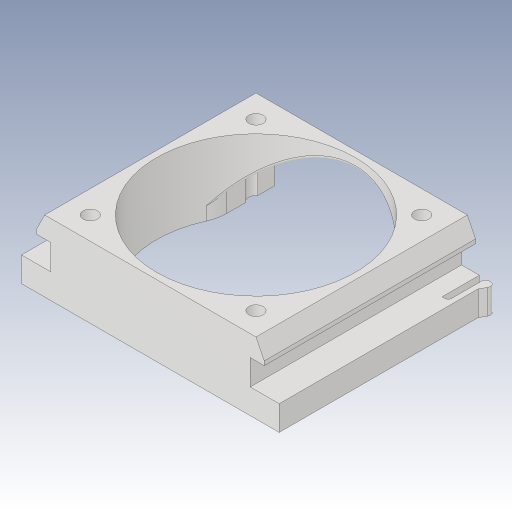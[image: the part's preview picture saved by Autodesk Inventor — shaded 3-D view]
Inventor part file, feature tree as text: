
AUTODESK INVENTOR PART (.ipt)
format: ipt  version: 2023.3 (Build 273359000, 359)  size: 267,264 bytes
history: native  units: in
note: dims shown in document units (in); Inventor stores cm internally (conversion verified against a paired STEP export)
features: extrude x5, sketch x5, fillet x3, plane x2, chamfer x2, hole x1, mirror x1, projected_geometry x1
ambient origin geometry x8: Origin, YZ Plane, XZ Plane, XY Plane, X Axis, Y Axis, Z Axis, Center Point
bodies: Body1 (feature_tree)
feature tree (20):
  extrude  "Extrusion3"  Depth=0.1211in
  plane  "Arbeitsebene1"
  extrude  "Extrusion4"  Depth=0.1378in
  chamfer  "Fase1"  Distance=1.0039in
  extrude  "Extrusion5"  Depth=0.8268in TaperAngle=0.0deg
  fillet  "Rundung1"  Radius=0.962in
  fillet  "Rundung2"  Radius=1.0827in
  hole  "Bohrung1"  [1 undecoded]
  sketch  "Skizze7"  dims[d20=0.9449in d21=0.502in d22=0.7874in d23=0.0in d27=0.1969in d28=0.0157in d29=0.7874in d30=0.0689in d31=0.1969in d32=0.119in d33=0.0787in d34=0.5635in d35=0.248in d36=0.0in d38=0.0531in d39=0.0236in d40=0.0394in d41=0.1772in d42=0.1181in d43=0.0in d44=0.1181in d45=0.0in d46=0.0157in d47=0.0197in d48=0.0787in d49=45.0deg]
  extrude  "Extrusion6"  Depth=0.0197in
  extrude  "Extrusion7"  Depth=0.0197in TaperAngle=0.0deg
  fillet  "Rundung3"  Radius=0.1969in
  plane  "Arbeitsebene2"
  mirror  "Spiegeln1"
  chamfer  "Fase3"  Distance=0.0157in
  sketch  "Skizze3"  dims[d4=0.9488in d5=0.1211in]
  sketch  "Skizze4"  dims[d6=0.1181in d7=0.1378in d8=1.0039in d9=0.0in]
  sketch  "Skizze5"  dims[d10=0.2953in d12=0.8268in d13=0.0in d14=0.962in d15=1.0827in]
  sketch  "Skizze6"  dims[d16=0.0984in d17=0.0394in d18=0.0787in d19=45.0deg]
  projected_geometry  "Projizierte Kontur1"
note: 1 required parameter value undecoded (feature->parameter linkage not recoverable at this tier; creation-order binding heuristic only, values carry confidence <= 0.55)
